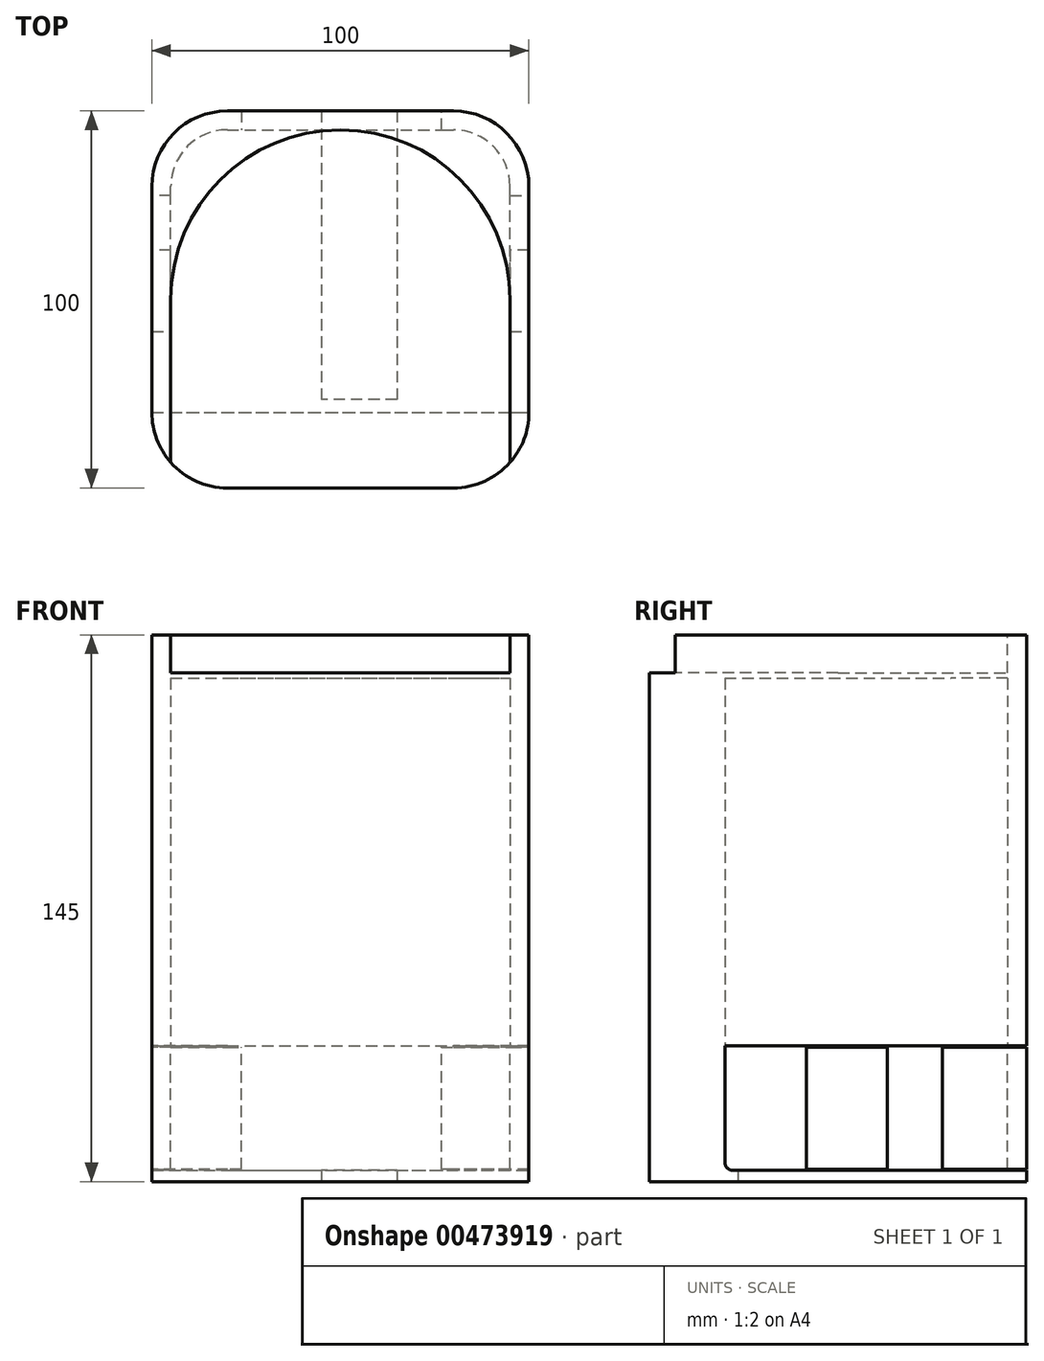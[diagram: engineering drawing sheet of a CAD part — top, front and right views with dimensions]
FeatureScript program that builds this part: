
annotation { "Feature Type Name" : "Feature", "Feature Type Description" : "" }
export const myFeature = defineFeature(function(context is Context, id is Id, definition is map)
    precondition{}
    {
        {
            var Q0;
            Q0=qCreatedBy(makeId("Top.planeOp"),FACE);
            var sketch = newSketch(context, id + "F0", { "sketchPlane" : qUnion([Q0])});
            skLineSegment(sketch, "E0.bottom", {"start": v(0, 0) * mm, "end": v(-100, 0) * mm});
            skLineSegment(sketch, "E0.top", {"start": v(0, 100) * mm, "end": v(-100, 100) * mm});
            skLineSegment(sketch, "E0.left", {"start": v(0, 0) * mm, "end": v(0, 100) * mm});
            skLineSegment(sketch, "E0.right", {"start": v(-100, 0) * mm, "end": v(-100, 100) * mm});
            skSolve(sketch);
        }
        {
            var Q0;
            Q0=makeQuery(id+"F0.imprint","IMPRINT",FACE,{"disambiguationData":[TD([[makeQuery(id+"F0.imprint","IMPRINT",EDGE,{"derivedFrom":sQuery(id+"F0.wireOp",EDGE,"E0.bottom")}),-1.0]])]});
            extrude(context, id + "F1", {"entities" : qUnion([Q0]), "depth" : 145 * mm});
        }
        {
            var Q0;
            Q0=makeQuery(id+"F1.opExtrude","CAP_FACE",FACE,{"disambiguationData":[OSD([sQuery(id+"F0.wireOp",EDGE,"E0.bottom"),sQuery(id+"F0.wireOp",EDGE,"E0.top"),sQuery(id+"F0.wireOp",EDGE,"E0.left"),sQuery(id+"F0.wireOp",EDGE,"E0.right")])],"isStart":false});
            var sketch = newSketch(context, id + "F2", { "sketchPlane" : qUnion([Q0])});
            skCircle(sketch, "E1", {"center": v(-50, 50) * mm, "radius": 45 * mm});
            skPoint(sketch, "E1.centerSnap0", {"position": v(-50, 0) * mm});
            skPoint(sketch, "E1.centerSnap1", {"position": v(-100, 50) * mm});
            skSolve(sketch);
        }
        {
            var Q0;
            Q0=makeQuery(id+"F2.imprint","IMPRINT",FACE,{"disambiguationData":[TD([[makeQuery(id+"F2.imprint","IMPRINT",EDGE,{"derivedFrom":sQuery(id+"F2.wireOp",EDGE,"E1")}),1.0]])]});
            extrude(context, id + "F3", {"entities" : qUnion([Q0]), "operationType" : NewBodyOperationType.REMOVE, "oppositeDirection" : true, "depth" : 10 * mm});
        }
        {
            var Q0;
            Q0=makeQuery(id+"F1.opExtrude","SWEPT_FACE",FACE,{"disambiguationData":[OSD([sQuery(id+"F0.wireOp",EDGE,"E0.top")])]});
            var sketch = newSketch(context, id + "F4", { "sketchPlane" : qUnion([Q0])});
            skLineSegment(sketch, "E2.bottom", {"start": v(100, 3) * mm, "end": v(0, 3) * mm});
            skLineSegment(sketch, "E2.top", {"start": v(100, 36) * mm, "end": v(0, 36) * mm});
            skLineSegment(sketch, "E2.left", {"start": v(100, 3) * mm, "end": v(100, 36) * mm});
            skLineSegment(sketch, "E2.right", {"start": v(0, 3) * mm, "end": v(0, 36) * mm});
            skSolve(sketch);
        }
        {
            var Q0;
            Q0=makeQuery(id+"F4.imprint","IMPRINT",FACE,{"disambiguationData":[TD([[makeQuery(id+"F4.imprint","IMPRINT",EDGE,{"derivedFrom":sQuery(id+"F4.wireOp",EDGE,"E2.bottom")}),-1.0]])]});
            extrude(context, id + "F5", {"entities" : qUnion([Q0]), "operationType" : NewBodyOperationType.REMOVE, "oppositeDirection" : true, "depth" : 80 * mm});
        }
        {
            var Q0;
            {var subQ0=sQuery(id+"F0.wireOp",EDGE,"E0.left");var subQ1=sQuery(id+"F0.wireOp",EDGE,"E0.top");Q0=makeQuery(id+"F5.boolean.opBoolean","SPLIT",EDGE,{"disambiguationData":[TD([makeQuery(id+"F5.opExtrude","SWEPT_FACE",FACE,{"disambiguationData":[OSD([sQuery(id+"F4.wireOp",EDGE,"E2.top")])]})])],"derivedFrom":makeQuery(id+"F1.opExtrude","SWEPT_EDGE",EDGE,{"disambiguationData":[OSD([subQ1,subQ0])]})});}
            var Q1;
            {var subQ0=sQuery(id+"F0.wireOp",EDGE,"E0.right");var subQ1=sQuery(id+"F0.wireOp",EDGE,"E0.top");Q1=makeQuery(id+"F5.boolean.opBoolean","SPLIT",EDGE,{"disambiguationData":[TD([makeQuery(id+"F5.opExtrude","SWEPT_FACE",FACE,{"disambiguationData":[OSD([sQuery(id+"F4.wireOp",EDGE,"E2.top")])]})])],"derivedFrom":makeQuery(id+"F1.opExtrude","SWEPT_EDGE",EDGE,{"disambiguationData":[OSD([subQ1,subQ0])]})});}
            var Q2;
            Q2=makeQuery(id+"F1.opExtrude","SWEPT_EDGE",EDGE,{"disambiguationData":[OSD([sQuery(id+"F0.wireOp",EDGE,"E0.bottom"),sQuery(id+"F0.wireOp",EDGE,"E0.right")])]});
            var Q3;
            Q3=makeQuery(id+"F1.opExtrude","SWEPT_EDGE",EDGE,{"disambiguationData":[OSD([sQuery(id+"F0.wireOp",EDGE,"E0.bottom"),sQuery(id+"F0.wireOp",EDGE,"E0.left")])]});
            var Q4;
            {var subQ0=sQuery(id+"F0.wireOp",EDGE,"E0.left");var subQ1=sQuery(id+"F0.wireOp",EDGE,"E0.top");Q4=makeQuery(id+"F5.boolean.opBoolean","SPLIT",EDGE,{"disambiguationData":[TD([makeQuery(id+"F5.opExtrude","SWEPT_FACE",FACE,{"disambiguationData":[OSD([sQuery(id+"F4.wireOp",EDGE,"E2.bottom")])]})])],"derivedFrom":makeQuery(id+"F1.opExtrude","SWEPT_EDGE",EDGE,{"disambiguationData":[OSD([subQ1,subQ0])]})});}
            var Q5;
            {var subQ0=sQuery(id+"F0.wireOp",EDGE,"E0.right");var subQ1=sQuery(id+"F0.wireOp",EDGE,"E0.top");Q5=makeQuery(id+"F5.boolean.opBoolean","SPLIT",EDGE,{"disambiguationData":[TD([makeQuery(id+"F5.opExtrude","SWEPT_FACE",FACE,{"disambiguationData":[OSD([sQuery(id+"F4.wireOp",EDGE,"E2.bottom")])]})])],"derivedFrom":makeQuery(id+"F1.opExtrude","SWEPT_EDGE",EDGE,{"disambiguationData":[OSD([subQ1,subQ0])]})});}
            fillet(context, id + "F6", {"entities" : qUnion([Q0, Q1, Q2, Q3, Q4, Q5]), "radius" : 20 * mm, "tangentPropagation" : true, "allowEdgeOverflow" : false});
        }
        {
            var Q0;
            Q0=makeQuery(id+"F5.boolean.opBoolean","COPY",FACE,{"derivedFrom":makeQuery(id+"F5.opExtrude","SWEPT_FACE",FACE,{"disambiguationData":[OSD([sQuery(id+"F4.wireOp",EDGE,"E2.top")])]})});
            var sketch = newSketch(context, id + "F7", { "sketchPlane" : qUnion([Q0])});
            skLineSegment(sketch, "E3.0", {"start": v(-80, -95) * mm, "end": v(-20, -95) * mm});
            skLineSegment(sketch, "E3.1", {"start": v(-5, -25) * mm, "end": v(-5, -80) * mm});
            skLineSegment(sketch, "E3.2", {"start": v(-95, -25) * mm, "end": v(-5, -25) * mm});
            skArc(sketch, "E3.3", {"start": v(-20, -95) * mm, "mid": v(-9.4, -90.6) * mm, "end": v(-5, -80) * mm});
            skLineSegment(sketch, "E3.4", {"start": v(-95, -25) * mm, "end": v(-95, -80) * mm});
            skArc(sketch, "E3.5", {"start": v(-95, -80) * mm, "mid": v(-90.6, -90.6) * mm, "end": v(-80, -95) * mm});
            skSolve(sketch);
        }
        {
            var Q0;
            Q0=makeQuery(id+"F7.imprint","IMPRINT",FACE,{"disambiguationData":[TD([[makeQuery(id+"F7.imprint","IMPRINT",EDGE,{"derivedFrom":sQuery(id+"F7.wireOp",EDGE,"E3.0")}),1.0]])]});
            extrude(context, id + "F8", {"entities" : qUnion([Q0]), "operationType" : NewBodyOperationType.REMOVE, "oppositeDirection" : true, "depth" : 97.5 * mm});
        }
        {
            var Q0;
            Q0 = qSketchRegion(id + "F4", true);
            var Q1;
            Q1=makeQuery(id+"F8.boolean.opBoolean","COPY",FACE,{"derivedFrom":makeQuery(id+"F8.opExtrude","SWEPT_FACE",FACE,{"disambiguationData":[OSD([sQuery(id+"F7.wireOp",EDGE,"E3.2")])]})});
            extrude(context, id + "F9", {"entities" : qUnion([Q0, Q1]), "operationType" : NewBodyOperationType.REMOVE, "oppositeDirection" : true, "depth" : 5 * mm});
        }
        {
            var Q0;
            Q0=makeQuery(id+"F5.boolean.opBoolean","COPY",FACE,{"derivedFrom":makeQuery(id+"F5.opExtrude","SWEPT_FACE",FACE,{"disambiguationData":[OSD([sQuery(id+"F4.wireOp",EDGE,"E2.top")])]})});
            var Q1;
            Q1=makeQuery(id+"F5.boolean.opBoolean","COPY",FACE,{"derivedFrom":makeQuery(id+"F5.opExtrude","SWEPT_FACE",FACE,{"disambiguationData":[OSD([sQuery(id+"F4.wireOp",EDGE,"E2.bottom")])]})});
            extrude(context, id + "F10", {"entities" : qUnion([Q0]), "endBound" : BoundingType.UP_TO_SURFACE, "endBoundEntityFace" : qUnion([Q1]), "depth" : 25 * mm});
        }
        {
            var Q0;
            Q0=makeQuery(id+"F10.opExtrude","CAP_FACE",FACE,{"disambiguationData":[OSD([sQuery(id+"F4.wireOp",EDGE,"E2.top")])],"isStart":true});
            extrude(context, id + "F11", {"entities" : qUnion([Q0]), "operationType" : NewBodyOperationType.REMOVE, "oppositeDirection" : true, "depth" : 0.3 * mm});
        }
        {
            var Q0;
            Q0=makeQuery(id+"F10.opExtrude","CAP_FACE",FACE,{"disambiguationData":[OSD([sQuery(id+"F4.wireOp",EDGE,"E2.top")])],"isStart":false});
            extrude(context, id + "F12", {"entities" : qUnion([Q0]), "operationType" : NewBodyOperationType.REMOVE, "oppositeDirection" : true, "depth" : 0.3 * mm});
        }
        {
            var Q0;
            Q0=makeQuery(id+"F11.boolean.opBoolean","COPY",FACE,{"derivedFrom":makeQuery(id+"F11.opExtrude","CAP_FACE",FACE,{"disambiguationData":[OSD([sQuery(id+"F4.wireOp",EDGE,"E2.top")])],"isStart":false})});
            var sketch = newSketch(context, id + "F13", { "sketchPlane" : qUnion([Q0])});
            skLineSegment(sketch, "E4", {"start": v(-100, 41.54) * mm, "end": v(-95, 41.54) * mm});
            skLineSegment(sketch, "E5", {"start": v(-95, 41.54) * mm, "end": v(-95, 63.06) * mm});
            skLineSegment(sketch, "E6", {"start": v(-95, 63.06) * mm, "end": v(-100, 63.06) * mm});
            skLineSegment(sketch, "E7", {"start": v(-100, 63.06) * mm, "end": v(-100, 41.54) * mm});
            skLineSegment(sketch, "E8", {"start": v(-5, 41.54) * mm, "end": v(0, 41.54) * mm});
            skLineSegment(sketch, "E9", {"start": v(0, 41.54) * mm, "end": v(0, 63.06) * mm});
            skLineSegment(sketch, "E10", {"start": v(0, 63.06) * mm, "end": v(-5, 63.06) * mm});
            skLineSegment(sketch, "E11", {"start": v(-5, 63.06) * mm, "end": v(-5, 41.54) * mm});
            skLineSegment(sketch, "E12", {"start": v(-23.2, 95) * mm, "end": v(-23.2, 100) * mm});
            skLineSegment(sketch, "E13", {"start": v(-23.2, 100) * mm, "end": v(-76.27, 100) * mm});
            skLineSegment(sketch, "E14", {"start": v(-76.27, 100) * mm, "end": v(-76.27, 95) * mm});
            skLineSegment(sketch, "E15", {"start": v(-76.27, 95) * mm, "end": v(-23.2, 95) * mm});
            skLineSegment(sketch, "E16", {"start": v(-95, 77.63) * mm, "end": v(-100, 77.63) * mm});
            skLineSegment(sketch, "E17", {"start": v(-100, 77.63) * mm, "end": v(-100, 63.06) * mm});
            skLineSegment(sketch, "E18", {"start": v(-95, 77.63) * mm, "end": v(-95, 63.06) * mm});
            skLineSegment(sketch, "E19", {"start": v(-5, 63.06) * mm, "end": v(-5, 77.63) * mm});
            skLineSegment(sketch, "E20", {"start": v(-5, 77.63) * mm, "end": v(0, 77.63) * mm});
            skLineSegment(sketch, "E21", {"start": v(0, 77.63) * mm, "end": v(0, 63.06) * mm});
            skSolve(sketch);
        }
        {
            var Q0;
            {var subQ0=sQuery(id+"F13.wireOp",EDGE,"E4");Q0=makeQuery(id+"F13.imprint","IMPRINT",FACE,{"disambiguationData":[TD([[makeQuery(id+"F13.imprint","IMPRINT",EDGE,{"derivedFrom":subQ0}),-1.0]])]});}
            var Q1;
            {var subQ0=sQuery(id+"F13.wireOp",EDGE,"E8");Q1=makeQuery(id+"F13.imprint","IMPRINT",FACE,{"disambiguationData":[TD([[makeQuery(id+"F13.imprint","IMPRINT",EDGE,{"derivedFrom":subQ0}),-1.0]])]});}
            var Q2;
            Q2=makeQuery(id+"F13.imprint","IMPRINT",FACE,{"disambiguationData":[TD([[makeQuery(id+"F13.imprint","IMPRINT",EDGE,{"derivedFrom":sQuery(id+"F13.wireOp",EDGE,"E12")}),1.0]])]});
            var Q3;
            Q3=makeQuery(id+"F13.imprint","IMPRINT",FACE,{"disambiguationData":[TD([[makeQuery(id+"F13.imprint","IMPRINT",EDGE,{"derivedFrom":sQuery(id+"F13.wireOp",EDGE,"E10")}),-1.0]])]});
            var Q4;
            Q4=makeQuery(id+"F13.imprint","IMPRINT",FACE,{"disambiguationData":[TD([[makeQuery(id+"F13.imprint","IMPRINT",EDGE,{"derivedFrom":sQuery(id+"F13.wireOp",EDGE,"E6")}),-1.0]])]});
            extrude(context, id + "F14", {"entities" : qUnion([Q0, Q1, Q2, Q3, Q4]), "operationType" : NewBodyOperationType.REMOVE, "endBound" : BoundingType.UP_TO_NEXT, "oppositeDirection" : true, "depth" : 25 * mm});
        }
        {
            var Q0;
            Q0=makeQuery(id+"F1.opExtrude","CAP_FACE",FACE,{"disambiguationData":[OSD([sQuery(id+"F0.wireOp",EDGE,"E0.bottom"),sQuery(id+"F0.wireOp",EDGE,"E0.top"),sQuery(id+"F0.wireOp",EDGE,"E0.left"),sQuery(id+"F0.wireOp",EDGE,"E0.right")])],"isStart":false});
            var sketch = newSketch(context, id + "F15", { "sketchPlane" : qUnion([Q0])});
            skLineSegment(sketch, "E22", {"start": v(-95, 50) * mm, "end": v(-95, 6.77) * mm});
            skLineSegment(sketch, "E23", {"start": v(-5, 50) * mm, "end": v(-5, 6.77) * mm});
            skSolve(sketch);
        }
        {
            var Q0;
            {var subQ7=sQuery(id+"F15.wireOp",EDGE,"E22");Q0=makeQuery(id+"F15.imprint","IMPRINT",FACE,{"disambiguationData":[TD([[makeQuery(id+"F15.imprint","IMPRINT",EDGE,{"derivedFrom":subQ7}),1.0]])]});}
            extrude(context, id + "F16", {"entities" : qUnion([Q0]), "operationType" : NewBodyOperationType.REMOVE, "oppositeDirection" : true, "depth" : 10 * mm});
        }
        {
            var Q0;
            Q0=makeQuery(id+"F1.opExtrude","CAP_FACE",FACE,{"disambiguationData":[OSD([sQuery(id+"F0.wireOp",EDGE,"E0.bottom"),sQuery(id+"F0.wireOp",EDGE,"E0.top"),sQuery(id+"F0.wireOp",EDGE,"E0.left"),sQuery(id+"F0.wireOp",EDGE,"E0.right")])],"isStart":true});
            var sketch = newSketch(context, id + "F17", { "sketchPlane" : qUnion([Q0])});
            skLineSegment(sketch, "E24.bottom", {"start": v(-35, -100) * mm, "end": v(-55, -100) * mm});
            skLineSegment(sketch, "E24.top", {"start": v(-35, -23.45) * mm, "end": v(-55, -23.45) * mm});
            skLineSegment(sketch, "E24.left", {"start": v(-35, -100) * mm, "end": v(-35, -23.45) * mm});
            skLineSegment(sketch, "E24.right", {"start": v(-55, -100) * mm, "end": v(-55, -23.45) * mm});
            skSolve(sketch);
        }
        {
            var Q0;
            Q0=makeQuery(id+"F17.imprint","IMPRINT",FACE,{"disambiguationData":[TD([[makeQuery(id+"F17.imprint","IMPRINT",EDGE,{"derivedFrom":sQuery(id+"F17.wireOp",EDGE,"E24.bottom")}),-1.0]])]});
            extrude(context, id + "F18", {"entities" : qUnion([Q0]), "operationType" : NewBodyOperationType.REMOVE, "endBound" : BoundingType.UP_TO_NEXT, "oppositeDirection" : true, "depth" : 25 * mm});
        }
        {
            var Q0;
            Q0=makeQuery(id+"F5.boolean.opBoolean","COPY",EDGE,{"derivedFrom":makeQuery(id+"F5.opExtrude","CAP_EDGE",EDGE,{"disambiguationData":[OSD([sQuery(id+"F4.wireOp",EDGE,"E2.bottom")])],"isStart":false})});
            fillet(context, id + "F19", {"entities" : qUnion([Q0]), "radius" : 2 * mm, "tangentPropagation" : true, "allowEdgeOverflow" : false});
        }
    });
